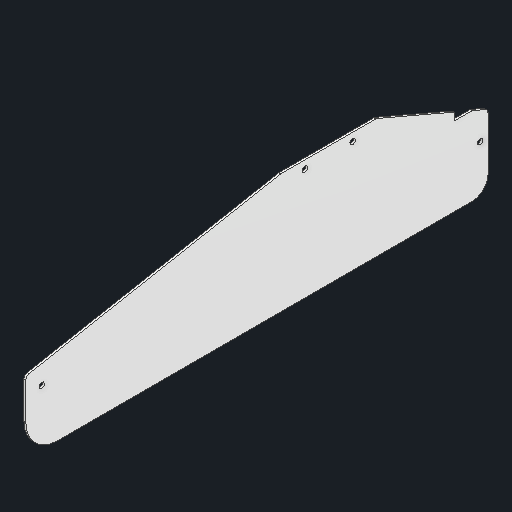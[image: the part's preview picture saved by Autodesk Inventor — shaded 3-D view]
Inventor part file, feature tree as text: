
AUTODESK INVENTOR PART (.ipt)
format: ipt  version: 2025 (Build 290162000, 162)  size: 167,936 bytes
history: native  units: in
note: dims shown in document units (in); Inventor stores cm internally (conversion verified against a paired STEP export)
features: other x5, sketch x1, extrude x1
ambient origin geometry x8: Origin, YZ Plane, XZ Plane, XY Plane, X Axis, Y Axis, Z Axis, Center Point
bodies: Solid1 (feature_tree)
feature tree (7):
  other  "Blocks"
  sketch  "Sketch1"  dims[d0=1.0in d1=0.125in d2=0.125in d3=0.125in d4=1.25in d5=90.0deg d6=1.0in d7=0.5in d8=0.0625in d9=0.0in d10=0.125in d11=0.2749in d16=0.5in d17=0.5625in]
  extrude  "Extrusion1"  Depth=0.0625in TaperAngle=0.0deg
  other  "Bend Part1"
  other  "main"
  other  "main:1"
  other  "Definition1"
